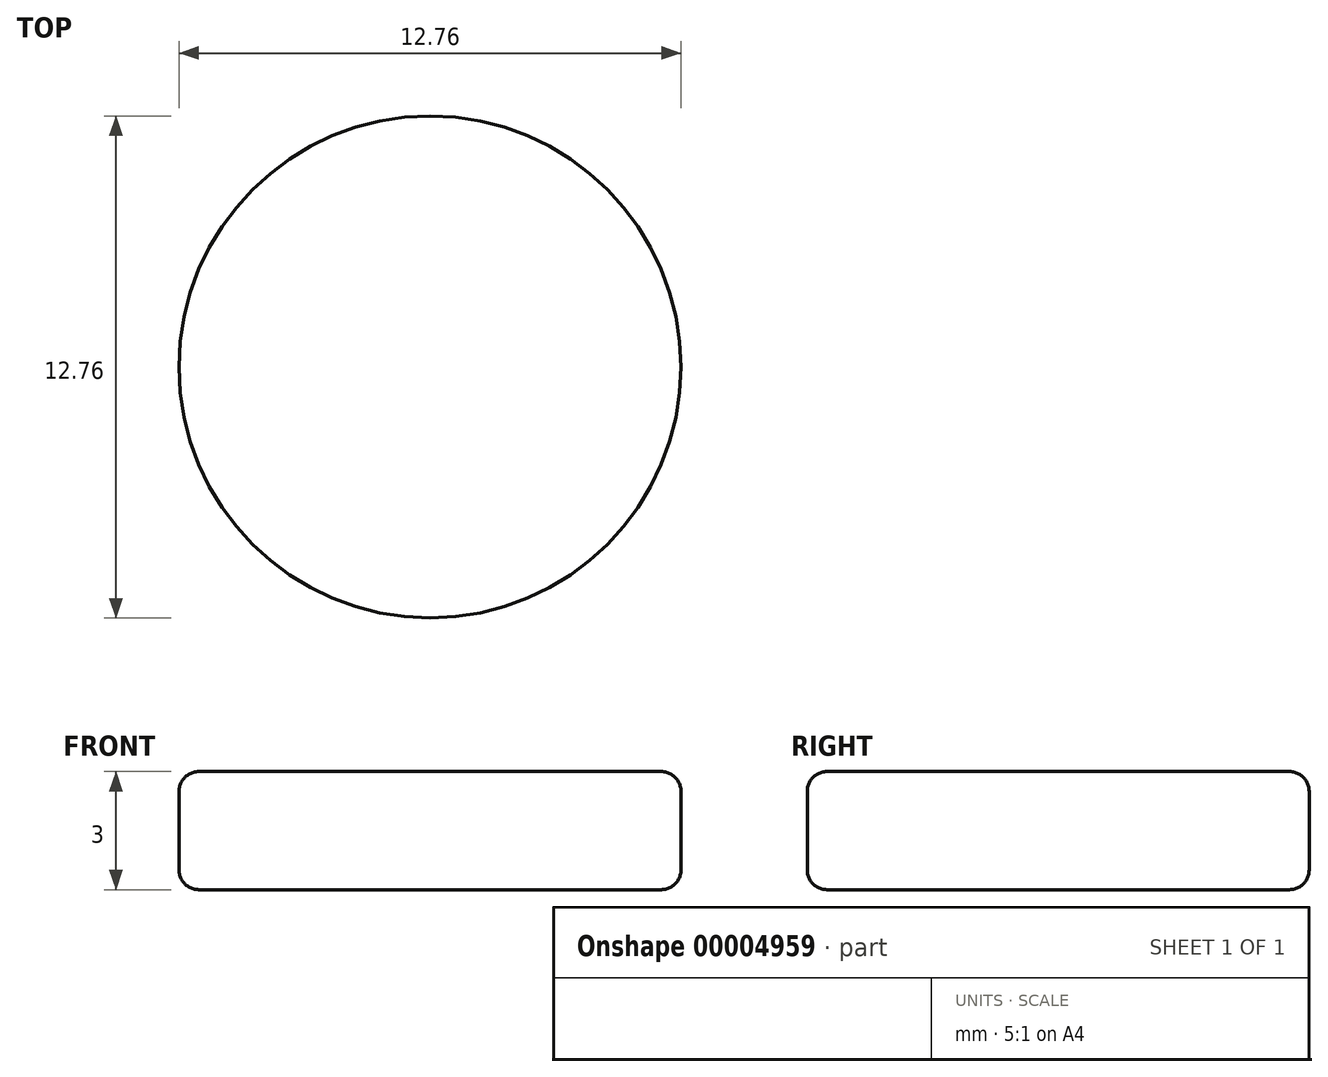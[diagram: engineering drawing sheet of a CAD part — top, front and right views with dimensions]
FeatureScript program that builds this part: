
annotation { "Feature Type Name" : "Feature", "Feature Type Description" : "" }
export const myFeature = defineFeature(function(context is Context, id is Id, definition is map)
    precondition{}
    {
        {
            var Q0;
            Q0=qCreatedBy(makeId("Top.planeOp"),FACE);
            var sketch = newSketch(context, id + "F0", { "sketchPlane" : qUnion([Q0])});
            skCircle(sketch, "E0", {"center": v(0, 0) * mm, "radius": 6.38 * mm});
            skSolve(sketch);
        }
        {
            var Q0;
            Q0 = qSketchRegion(id + "F0", true);
            extrude(context, id + "F1", {"entities" : qUnion([Q0]), "depth" : 3 * mm});
        }
        {
            var Q0;
            Q0=makeQuery(id+"F1.opExtrude","CAP_EDGE",EDGE,{"disambiguationData":[OSD([sQuery(id+"F0.wireOp",EDGE,"E0")])],"isStart":false});
            var Q1;
            Q1=makeQuery(id+"F1.opExtrude","CAP_EDGE",EDGE,{"disambiguationData":[OSD([sQuery(id+"F0.wireOp",EDGE,"E0")])],"isStart":true});
            fillet(context, id + "F2", {"entities" : qUnion([Q0, Q1]), "radius" : 0.5 * mm, "tangentPropagation" : true, "allowEdgeOverflow" : false});
        }
    });
